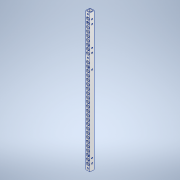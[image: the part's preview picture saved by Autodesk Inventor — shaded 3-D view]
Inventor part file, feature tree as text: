
AUTODESK INVENTOR PART (.ipt)
format: ipt  version: 2020.3 (Build 243373000, 373)  size: 254,464 bytes
history: native  units: mm
features: sketch x10, hole x9, other x1, extrude x1
ambient origin geometry x8: Origin, YZ Plane, XZ Plane, XY Plane, X Axis, Y Axis, Z Axis, Center Point
bodies: Body1 (feature_tree)
feature tree (21):
  other  "ソリッド1"
  extrude  "押し出し1"  Depth=9.0mm
  hole  "穴1"  [1 undecoded]
  hole  "穴2"  [1 undecoded]
  hole  "穴3"  [1 undecoded]
  hole  "穴4"  [1 undecoded]
  hole  "穴5"  [1 undecoded]
  hole  "穴6"  [1 undecoded]
  hole  "穴7"  [1 undecoded]
  hole  "穴8"  [1 undecoded]
  hole  "穴9"  [1 undecoded]
  sketch  "スケッチ1"
  sketch  "スケッチ2"
  sketch  "スケッチ3"
  sketch  "スケッチ4"
  sketch  "スケッチ5"
  sketch  "スケッチ6"
  sketch  "スケッチ7"
  sketch  "スケッチ8"
  sketch  "スケッチ9"
  sketch  "スケッチ10"
note: 9 required parameter values undecoded (feature->parameter linkage not recoverable at this tier; creation-order binding heuristic only, values carry confidence <= 0.55)
